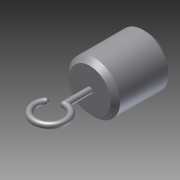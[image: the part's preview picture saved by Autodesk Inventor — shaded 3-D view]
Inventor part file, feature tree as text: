
AUTODESK INVENTOR PART (.ipt)
format: ipt  version: 2012 SP2 (Build 160219200, 219)  size: 153,600 bytes
history: native  units: in
note: dims shown in document units (in); Inventor stores cm internally (conversion verified against a paired STEP export)
features: sketch x4, extrude x2, chamfer x2, sweep x1, fillet x1, reference x1
ambient origin geometry x8: Origin, YZ Plane, XZ Plane, XY Plane, X Axis, Y Axis, Z Axis, Center Point
bodies: Solid1 (feature_tree)
feature tree (11):
  extrude  "Extrusion1"  Depth=1.781in TaperAngle=0.0deg
  extrude  "Extrusion2"  Depth=0.1412in TaperAngle=45.0deg
  chamfer  "Chamfer1"  Distance=0.1412in Angle=45.0deg
  chamfer  "Chamfer2"  [1 undecoded]
  sweep  "Sweep1"
  fillet  "Fillet1"  [1 undecoded]
  sketch  "Sketch1"  dims[d0=1.5748in d1=1.781in d2=0.0in]
  reference  "Reference1"
  sketch  "Sketch2"  dims[d3=0.7185in d4=0.0in d5=0.1412in d6=0.0787in d7=45.0deg d8=0.1412in d9=0.0787in d10=45.0deg]
  sketch  "Sketch3"  dims[d11=0.0in]
  sketch  "Sketch4"  dims[d12=0.0787in]
note: 2 required parameter values undecoded (feature->parameter linkage not recoverable at this tier; creation-order binding heuristic only, values carry confidence <= 0.55)
